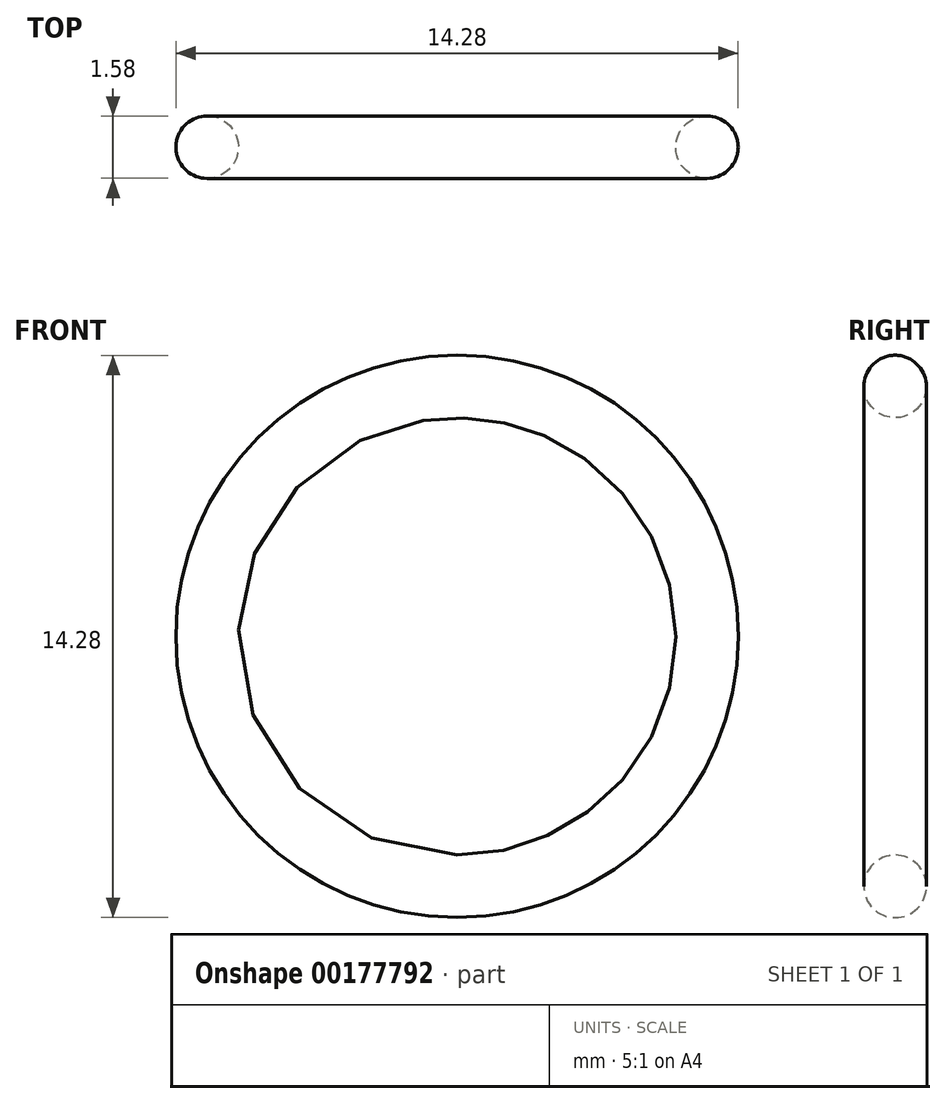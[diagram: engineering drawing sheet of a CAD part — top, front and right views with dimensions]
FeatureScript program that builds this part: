
annotation { "Feature Type Name" : "Feature", "Feature Type Description" : "" }
export const myFeature = defineFeature(function(context is Context, id is Id, definition is map)
    precondition{}
    {
        {
            var Q0;
            Q0=qCreatedBy(makeId("Front.planeOp"),FACE);
            var sketch = newSketch(context, id + "F0", { "sketchPlane" : qUnion([Q0])});
            skCircle(sketch, "E0", {"center": v(0, 0) * mm, "radius": 6.35 * mm});
            skSolve(sketch);
        }
        {
            var Q0;
            Q0=qCreatedBy(makeId("Right.planeOp"),FACE);
            var sketch = newSketch(context, id + "F1", { "sketchPlane" : qUnion([Q0])});
            skCircle(sketch, "E1", {"center": v(0, 6.35) * mm, "radius": 0.8 * mm});
            skSolve(sketch);
        }
        {
            var Q0;
            Q0=makeQuery(id+"F1.imprint","IMPRINT",FACE,{"disambiguationData":[TD([[makeQuery(id+"F1.imprint","IMPRINT",EDGE,{"derivedFrom":sQuery(id+"F1.wireOp",EDGE,"E1")}),1.0]])]});
            var Q1;
            Q1=sQuery(id+"F0.wireOp",EDGE,"E0");
            sweep(context, id + "F2", {"profiles" : qUnion([Q0]), "path" : qUnion([Q1])});
        }
    });
